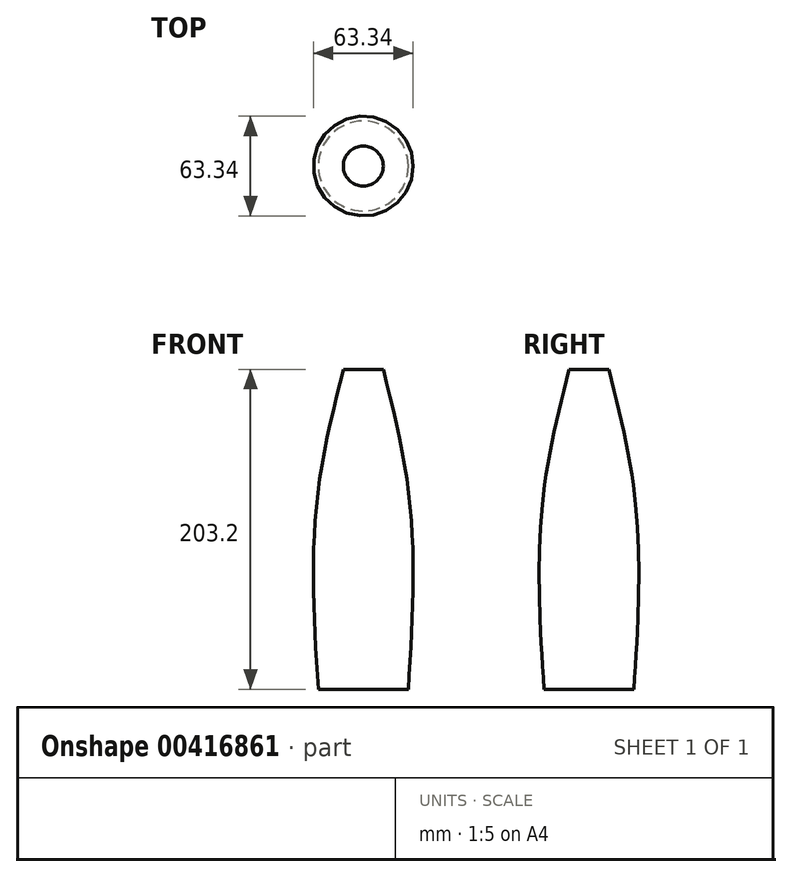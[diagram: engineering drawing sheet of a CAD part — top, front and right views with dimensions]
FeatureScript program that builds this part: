
annotation { "Feature Type Name" : "Feature", "Feature Type Description" : "" }
export const myFeature = defineFeature(function(context is Context, id is Id, definition is map)
    precondition{}
    {
        {
            var Q0;
            Q0=qCreatedBy(makeId("Top.planeOp"),FACE);
            var sketch = newSketch(context, id + "F0", { "sketchPlane" : qUnion([Q0])});
            skCircle(sketch, "E0", {"center": v(0, 0) * mm, "radius": 28.58 * mm});
            skSolve(sketch);
        }
        {
            var Q0;
            Q0=qCreatedBy(makeId("Top.planeOp"),FACE);
            cPlane(context, id + "F1", {"entities" : qUnion([Q0]), "cplaneType" : CPlaneType.OFFSET, "offset" : 127 * mm, "width" : 152.4 * mm, "height" : 152.4 * mm});
        }
        {
            var Q0;
            Q0=qCreatedBy(id+"F1.planeOp",FACE);
            var sketch = newSketch(context, id + "F2", { "sketchPlane" : qUnion([Q0])});
            skCircle(sketch, "E1", {"center": v(0, 0) * mm, "radius": 28.58 * mm});
            skSolve(sketch);
        }
        {
            var Q0;
            Q0=qCreatedBy(id+"F1.planeOp",FACE);
            cPlane(context, id + "F3", {"entities" : qUnion([Q0]), "cplaneType" : CPlaneType.OFFSET, "offset" : 76.2 * mm, "width" : 152.4 * mm, "height" : 152.4 * mm});
        }
        {
            var Q0;
            Q0=qCreatedBy(id+"F3.planeOp",FACE);
            var sketch = newSketch(context, id + "F4", { "sketchPlane" : qUnion([Q0])});
            skCircle(sketch, "E2", {"center": v(0, 0) * mm, "radius": 12.7 * mm});
            skSolve(sketch);
        }
        {
            var Q0;
            Q0=makeQuery(id+"F0.imprint","IMPRINT",FACE,{"disambiguationData":[TD([[makeQuery(id+"F0.imprint","IMPRINT",EDGE,{"derivedFrom":sQuery(id+"F0.wireOp",EDGE,"E0")}),1.0]])]});
            var Q1;
            Q1=makeQuery(id+"F2.imprint","IMPRINT",FACE,{"disambiguationData":[TD([[makeQuery(id+"F2.imprint","IMPRINT",EDGE,{"derivedFrom":sQuery(id+"F2.wireOp",EDGE,"E1")}),1.0]])]});
            var Q2;
            Q2=makeQuery(id+"F4.imprint","IMPRINT",FACE,{"disambiguationData":[TD([[makeQuery(id+"F4.imprint","IMPRINT",EDGE,{"derivedFrom":sQuery(id+"F4.wireOp",EDGE,"E2")}),1.0]])]});
            loft(context, id + "F5", {"sheetProfilesArray" : [{ "sheetProfileEntities" : qUnion([Q0]) }, { "sheetProfileEntities" : qUnion([Q1]) }, { "sheetProfileEntities" : qUnion([Q2]) }]});
        }
    });
